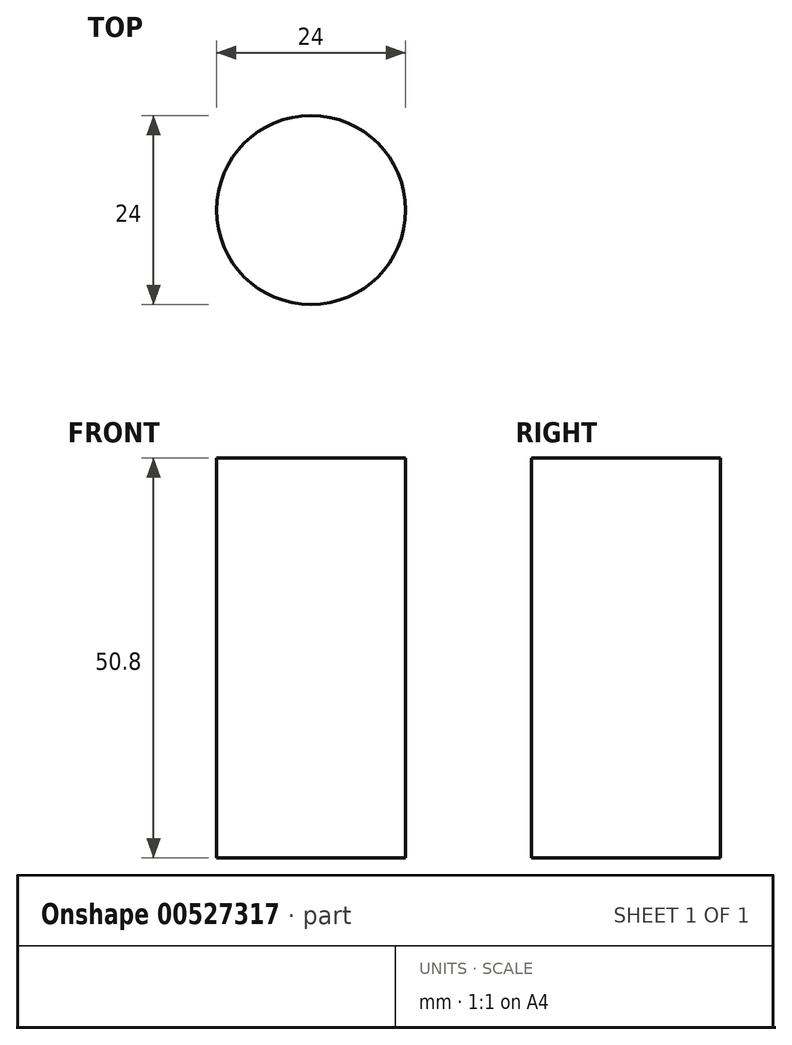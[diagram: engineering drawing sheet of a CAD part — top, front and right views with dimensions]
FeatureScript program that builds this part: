
annotation { "Feature Type Name" : "Feature", "Feature Type Description" : "" }
export const myFeature = defineFeature(function(context is Context, id is Id, definition is map)
    precondition{}
    {
        {
            var Q0;
            Q0=qCreatedBy(makeId("Top.planeOp"),FACE);
            var sketch = newSketch(context, id + "F0", { "sketchPlane" : qUnion([Q0])});
            skCircle(sketch, "E0", {"center": v(-27.04, 0) * mm, "radius": 12 * mm});
            skSolve(sketch);
        }
        {
            var Q0;
            Q0 = qSketchRegion(id + "F0", true);
            extrude(context, id + "F1", {"entities" : qUnion([Q0]), "oppositeDirection" : true, "depth" : 50.8 * mm, "offsetDistance" : 25.4 * mm});
        }
    });
